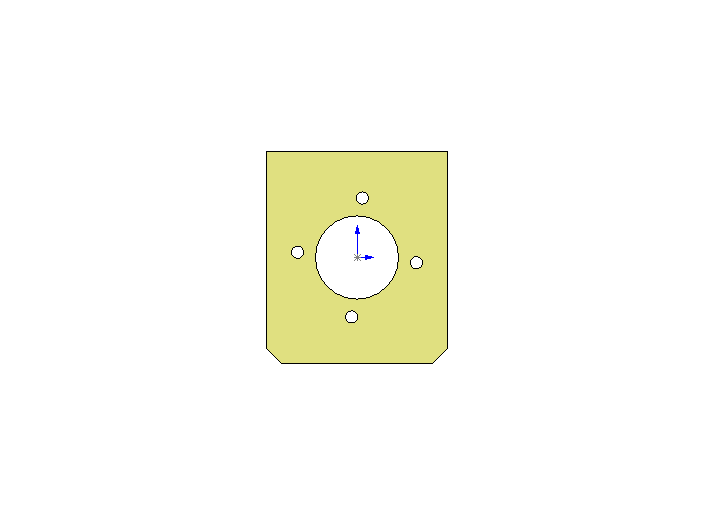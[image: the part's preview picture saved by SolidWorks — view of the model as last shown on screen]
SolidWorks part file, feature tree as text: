
SOLIDWORKS PART (.sldprt)
format: sldprt  version: not decoded by parser v0  size: 209,920 bytes
history: native  units: mm
features: sketch x3, extrude x1, chamfer x1, hole x1 (+10 scaffold rows collapsed)
feature tree (16):
  scaffold x10  (default folders/planes/origin — collapsed)
  sketch  "Sketch1"  dims[D1=76.2mm D2=88.9mm]
  extrude  "Extrude1"  Depth=7.9375mm
  chamfer  "Chamfer1"  Distance=6.35mm Angle=45deg
  hole  "#10 Clearance Hole2"  Diameter=5.1054mm Depth=7.9375mm
  sketch  "Sketch5"
  sketch  "Sketch4"  dims[hole-wizard template sketch: 60 standard entries collapsed; hole parameters kept: c18.Thru Hole Depth=7.9375mm]
decode coverage: 5 of 6 modeling features carry decoded parameters
note: ~ marks probable driven/reference dimensions
note: suppression state not decoded; provenance and decode notes live in map.json
